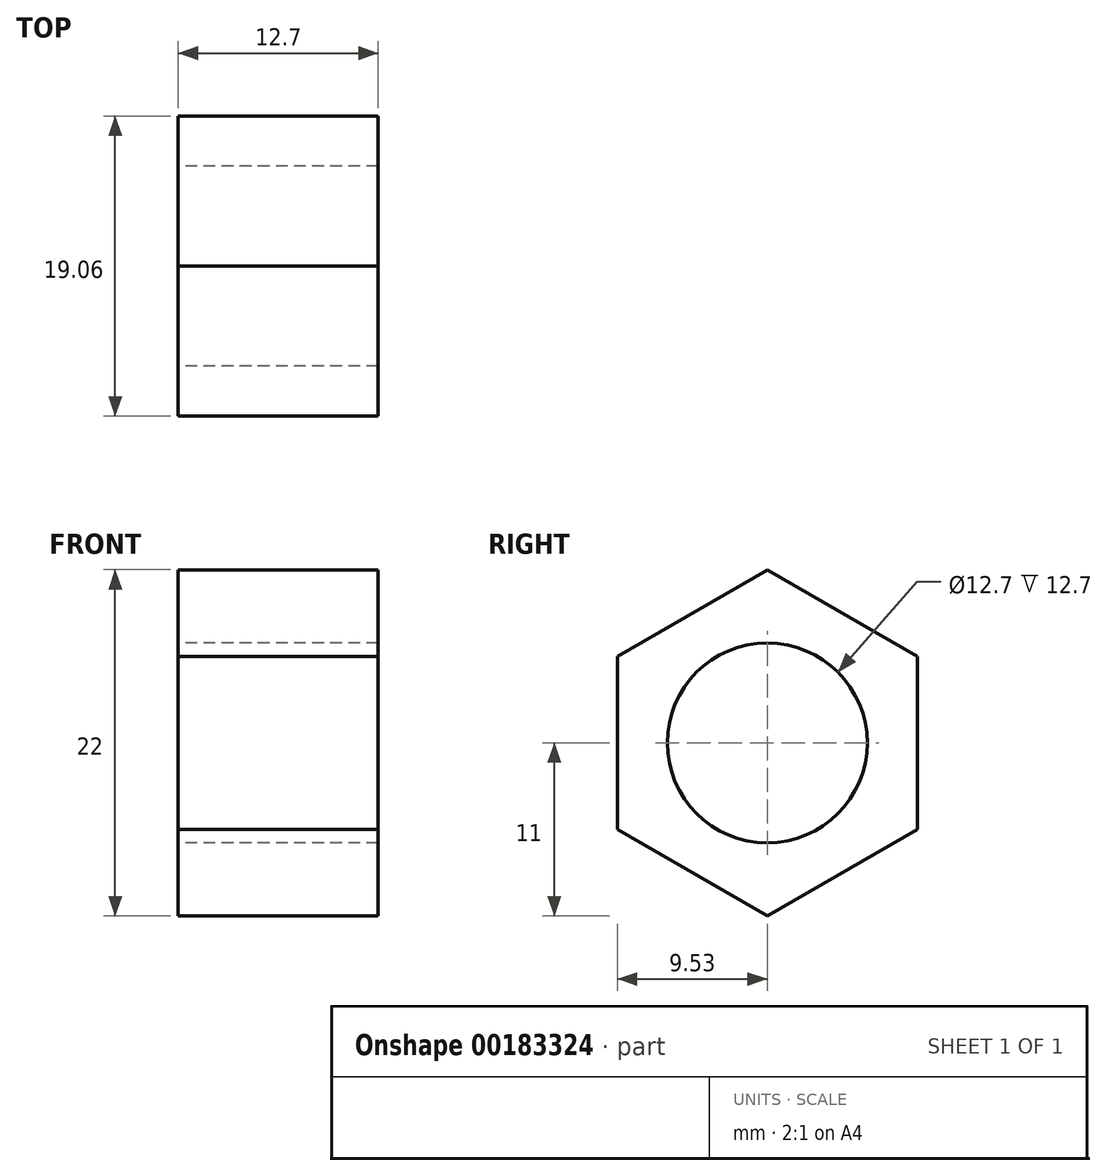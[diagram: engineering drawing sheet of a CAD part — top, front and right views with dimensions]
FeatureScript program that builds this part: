
annotation { "Feature Type Name" : "Feature", "Feature Type Description" : "" }
export const myFeature = defineFeature(function(context is Context, id is Id, definition is map)
    precondition{}
    {
        {
            var Q0;
            Q0=qCreatedBy(makeId("Right.planeOp"),FACE);
            var sketch = newSketch(context, id + "F0", { "sketchPlane" : qUnion([Q0])});
            skCircle(sketch, "E0.cCircle", {"center": v(0, 0) * mm, "radius": 9.53 * mm, "construction": true});
            skLineSegment(sketch, "E0.0", {"start": v(9.53, 5.5) * mm, "end": v(9.53, -5.5) * mm});
            skLineSegment(sketch, "E0.1", {"start": v(9.52, -5.5) * mm, "end": v(0, -11) * mm});
            skLineSegment(sketch, "E0.2", {"start": v(0, -11) * mm, "end": v(-9.53, -5.5) * mm});
            skLineSegment(sketch, "E0.3", {"start": v(-9.52, -5.5) * mm, "end": v(-9.53, 5.5) * mm});
            skLineSegment(sketch, "E0.4", {"start": v(-9.52, 5.5) * mm, "end": v(0, 11) * mm});
            skLineSegment(sketch, "E0.5", {"start": v(0, 11) * mm, "end": v(9.52, 5.5) * mm});
            skPoint(sketch, "E0.0.midPoint", {"position": v(9.53, 0) * mm});
            skSolve(sketch);
        }
        {
            var Q0;
            Q0 = qSketchRegion(id + "F0", true);
            extrude(context, id + "F1", {"entities" : qUnion([Q0]), "endBound" : BoundingType.SYMMETRIC, "depth" : 12.7 * mm});
        }
        {
            var Q0;
            Q0=makeQuery(id+"F1.opExtrude","CAP_FACE",FACE,{"disambiguationData":[OSD([sQuery(id+"F0.wireOp",EDGE,"E0.0"),sQuery(id+"F0.wireOp",EDGE,"E0.1"),sQuery(id+"F0.wireOp",EDGE,"E0.2"),sQuery(id+"F0.wireOp",EDGE,"E0.3"),sQuery(id+"F0.wireOp",EDGE,"E0.4"),sQuery(id+"F0.wireOp",EDGE,"E0.5")])],"isStart":false});
            var sketch = newSketch(context, id + "F2", { "sketchPlane" : qUnion([Q0])});
            skCircle(sketch, "E1", {"center": v(0, 0) * mm, "radius": 6.35 * mm});
            skSolve(sketch);
        }
        {
            var Q0;
            Q0 = qSketchRegion(id + "F2", true);
            extrude(context, id + "F3", {"entities" : qUnion([Q0]), "operationType" : NewBodyOperationType.REMOVE, "endBound" : BoundingType.SYMMETRIC, "depth" : 25.4 * mm});
        }
    });
